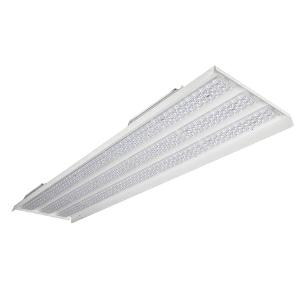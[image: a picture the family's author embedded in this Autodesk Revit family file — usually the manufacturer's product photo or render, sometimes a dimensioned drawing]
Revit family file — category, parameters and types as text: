
# Revit family: 3f_filippi_-_kit_led_retrofit_beta_430_3x_3f_filippi_-_a5311_-_kit_led_beta_430_-_l1551-_3x65w_ampio
name_source: partatom
category: Lighting Fixtures
units: mm (PartAtom-declared; Revit-internal decimal feet)

## family parameters
Cut with Voids When Loaded = No
Host = Face
Light Source = No
Part Type = Normal
Room Calculation Point = No
Round Connector Dimension = Use Diameter
Shared = No

## types (1)
- 3F Filippi - Kit LED Retrofit Beta 430 3X (1 x LED, 28294 lm, 173 W, 4000 K)
    Apparent Load = 173 VA
    Approval mark = ENEC
    CIE Flux Codes = 63 95 100 100 100
    Color Rendering = 80
    Color Temperature = 4000 K
    Control Gear = Electronic ballast
    Default Elevation = 1800 mm
    Description = Beta 430 Retrofit Kit to replace the 4x80W T5 Amalgam version

ILLUMINOTECHNICAL
Luminous efficiency 100% (DLOR 100%, ULOR 0%).
Initial luminous flux of the luminaire 28294 lm.
Wide symmetric distribution.
Installation Interdistance Transv.D = 1.52 x hu - Long.D = 1.55 x hu.
Tabular UGR (CIE 117 - 4H-8H; S=0.25H; 70/50/20): RUG 20.7 - 21.2.
Beam angle: 101° - 100°.
Luminous efficacy 164 lm/W.
Lifetime (L93/B10): 30000 h. (tq+25°C)
Lifetime (L90/B10): 50000 h. (tq+25°C)
Lifetime (L85/B10): 80000 h. (tq+25°C)
Lifetime (L80/B10): 100000 h. (tq+25°C)
Lifetime (L85/B10): 50000 h. (tq+40°C)
Sudden decreased luminous flux after 50000 hours: 0% (C0).
Photobiological safety in compliance with IEC/TR 62778: RG0 risk exempt, (IEC 62471).
In compliance with IEC/EN 62722-2-1 - IEC/EN 62717 standards.

SOURCE
3 linear LED modules 65W/840.
Energy efficiency class (UE 2019/2020 - UE 2019/2015): C.
CIE 13.3 Colour rendering index: CRI >80 (R9 <50%).
IES TM-30 Fidelity Index: Rf = 84 Rg = 95.
CCT nominal colour temperature 4000 K.
Colour initial tolerance (MacAdam): SDCM 3.

MECHANICAL
Gear-tray unit hot-galvanised steel, painted in white polyester.
Methacrylate (PMMA) lenses with external flat surface.
Luminaire with limited surface temperature. - D - (EN 60598-2-24)
Dimensions: 1551x430 mm, height 159 mm. Weight 6.225 kg.
Glow-wire test resistance 850°C.

ELECTRICAL
Halogen Free electronic wiring 230V-50/60Hz, power factor 0.97, THD <25%, constant output current, class I, 2 driver.
Twin-circuit.
Power of the luminaire 173 W.
CE - IEC 60598-1 - EN 60598-1.
SAFE FLICKER: PstLM=<1 and SVM=<0.4 (IEC TR 61547-1 and IEC TR 63158), to ensure a more comfortable and safe light.
Luminaire compliant with EN 60598-2-22 for power supply from a centralised emergency system CPSS (Central Power Supply System), not incorporated in the luminaire - high risk areas excluded. The default power and flux are 100% in AC and 100% in DC.
Ambient temperature from -20°C to +40°C.
Temperature class T6 max 85°C.
Relative humidity UR: <85%.

INSTALLATION
Retrofit.
Correct installation of the retrofit LED kit, compliant with EN 60598-1 and CE marked, inside the 3F Filippi - Beta 4x and 6x i3F 76 Fluorescent luminaires must be only carried out by qualified personnel to ensure compliance with the national installation standards.
Attention: to maintain the degree of protection of the device and for the purposes of validity of the guarantee of the new retrofit kits, it is imperative to replace the old cable guides (on the body of the device) with the new ones supplied.
All accessories dedicated to this product are available on the Catalog and on our website www.3F-Filippi.com.

WARNING
Fixture not suitable for cold stores with an ambient temperature <0°C and/or relative humidity >85%.
Luminaire designed for disposal/recycling at end-of-life.
Replaceable (LED only) light source by a professional. Replaceable control gear by a professional.
    Height = 159 mm
    Lamp = 1 x LED
    Lamp Light Flux = 28294 lm
    Lamp Power = 173 W
    Lamp count = 1
    Length = 1551 mm
    Lifetime = 50000 h
    Luminous efficacy = 164 lm/W
    Manufacturer = 3F Filippi
    ModVariant = No
    Model = 3F Filippi - A5311 - Kit LED Beta 430 - L1551- 3X65W AMPIO
    Mounting Place = Ceiling
    Mounting Type = Surface mounted
    Number of Poles = 1
    OnlyDefault = Yes
    Power Factor = 1
    Product Name = 3F Filippi - Kit LED Retrofit Beta 430 3X
    Product group = ceiling mounted luminaire
    ProductGroupID = 3
    Protection Class = Protection class I
    Protection Degree = Degree of protection
    RLX_Detail_Level = 1
    RLX_Emergency_Light_Flux = 0 lm
    RLX_Emergency_Type = 0
    RLX_Emergency_Type_DB = No
    RlxData = <blob elided: 58525 chars, md5=0e9a247a>
    Socket = socket
    Standby Power = 0 W
    System Light Flux = 28294 lm
    System Power = 173 W
    Type Comments = Product without accessories
    Type Image = 3ffilippi_a5311.jpg
    URL = http://relux.com
    VarID = ---
    Voltage = 0 V
    Weight = 0.00 kg
    Width = 430 mm

## geometry (parser evidence)
native form markers: Blend x4, Sweep x12
no freeform markers — native parametric forms only
